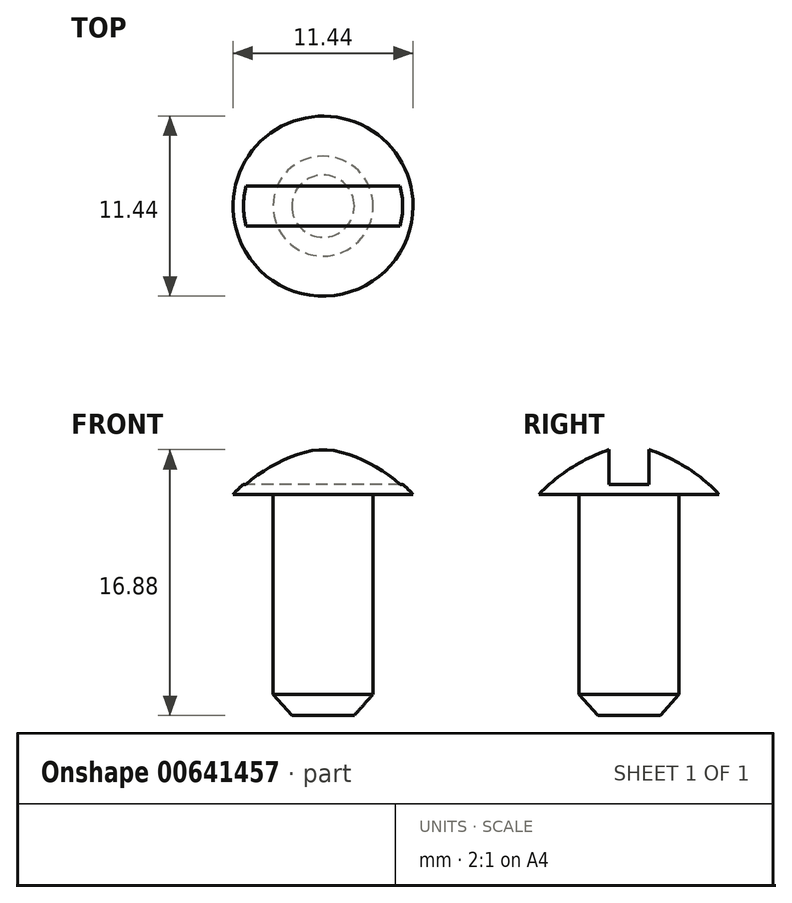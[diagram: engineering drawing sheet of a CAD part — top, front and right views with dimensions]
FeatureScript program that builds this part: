
annotation { "Feature Type Name" : "Feature", "Feature Type Description" : "" }
export const myFeature = defineFeature(function(context is Context, id is Id, definition is map)
    precondition{}
    {
        {
            var Q0;
            Q0=qCreatedBy(makeId("Front.planeOp"),FACE);
            var sketch = newSketch(context, id + "F0", { "sketchPlane" : qUnion([Q0])});
            skLineSegment(sketch, "E0", {"start": v(0, 0) * mm, "end": v(3.17, 0) * mm});
            skLineSegment(sketch, "E1", {"start": v(3.17, 0) * mm, "end": v(3.17, 12.7) * mm});
            skLineSegment(sketch, "E2", {"start": v(3.17, 12.7) * mm, "end": v(5.72, 12.7) * mm});
            skArc(sketch, "E3", {"start": v(5.72, 12.7) * mm, "mid": v(3.1, 14.72) * mm, "end": v(0, 15.88) * mm});
            skLineSegment(sketch, "E4", {"start": v(0, 15.88) * mm, "end": v(0, 0) * mm});
            skSolve(sketch);
        }
        {
            var Q0;
            Q0=makeQuery(id+"F0.imprint","IMPRINT",FACE,{"disambiguationData":[TD([[makeQuery(id+"F0.imprint","IMPRINT",EDGE,{"derivedFrom":sQuery(id+"F0.wireOp",EDGE,"E0")}),1.0]])]});
            var Q1;
            Q1=sQuery(id+"F0.wireOp",EDGE,"E4");
            revolve(context, id + "F1", {"entities" : qUnion([Q0]), "axis" : qUnion([Q1]), "revolveType" : RevolveType.FULL});
        }
        {
            var Q0;
            Q0=makeQuery(id+"F1.opRevolve","SWEPT_FACE",FACE,{"disambiguationData":[OSD([sQuery(id+"F0.wireOp",EDGE,"E0")])]});
            cPlane(context, id + "F2", {"entities" : qUnion([Q0]), "cplaneType" : CPlaneType.OFFSET, "offset" : 1.35 * mm, "width" : 152.4 * mm, "height" : 152.4 * mm});
        }
        {
            var Q0;
            Q0=qCreatedBy(id+"F2.planeOp",FACE);
            var sketch = newSketch(context, id + "F3", { "sketchPlane" : qUnion([Q0])});
            skCircle(sketch, "E5", {"center": v(0, 0) * mm, "radius": 1.98 * mm});
            skSolve(sketch);
        }
        {
            var Q1;
            Q1=makeQuery(id+"F1.opRevolve","SWEPT_FACE",FACE,{"disambiguationData":[OSD([sQuery(id+"F0.wireOp",EDGE,"E0")])]});
            var Q2;
            Q2=makeQuery(id+"F3.imprint","IMPRINT",FACE,{"disambiguationData":[TD([[makeQuery(id+"F3.imprint","IMPRINT",EDGE,{"derivedFrom":sQuery(id+"F3.wireOp",EDGE,"E5")}),1.0]])]});
            loft(context, id + "F4", {"operationType" : NewBodyOperationType.ADD, "sheetProfilesArray" : [{ "sheetProfileEntities" : qUnion([Q1]) }, { "sheetProfileEntities" : qUnion([Q2]) }]});
        }
        {
            var Q0;
            Q0=makeQuery(id+"F1.opRevolve","SWEPT_FACE",FACE,{"disambiguationData":[OSD([sQuery(id+"F0.wireOp",EDGE,"E2")])]});
            cPlane(context, id + "F5", {"entities" : qUnion([Q0]), "cplaneType" : CPlaneType.OFFSET, "offset" : 0.64 * mm, "oppositeDirection" : true, "width" : 152.4 * mm, "height" : 152.4 * mm});
        }
        {
            var Q0;
            Q0=qCreatedBy(id+"F5.planeOp",FACE);
            var sketch = newSketch(context, id + "F6", { "sketchPlane" : qUnion([Q0])});
            skLineSegment(sketch, "E6.bottom", {"start": v(5.08, -1.27) * mm, "end": v(-5.08, -1.27) * mm});
            skLineSegment(sketch, "E6.top", {"start": v(5.08, 1.27) * mm, "end": v(-5.08, 1.27) * mm});
            skLineSegment(sketch, "E6.left", {"start": v(5.08, -1.27) * mm, "end": v(5.08, 1.27) * mm});
            skLineSegment(sketch, "E6.right", {"start": v(-5.08, -1.27) * mm, "end": v(-5.08, 1.27) * mm});
            skPoint(sketch, "E6.middle", {"position": v(0, 0) * mm});
            skSolve(sketch);
        }
        {
            var Q0;
            Q0 = qSketchRegion(id + "F6", true);
            extrude(context, id + "F7", {"entities" : qUnion([Q0]), "operationType" : NewBodyOperationType.REMOVE, "oppositeDirection" : true, "depth" : 9.58 * mm, "offsetDistance" : 25.4 * mm});
        }
    });
